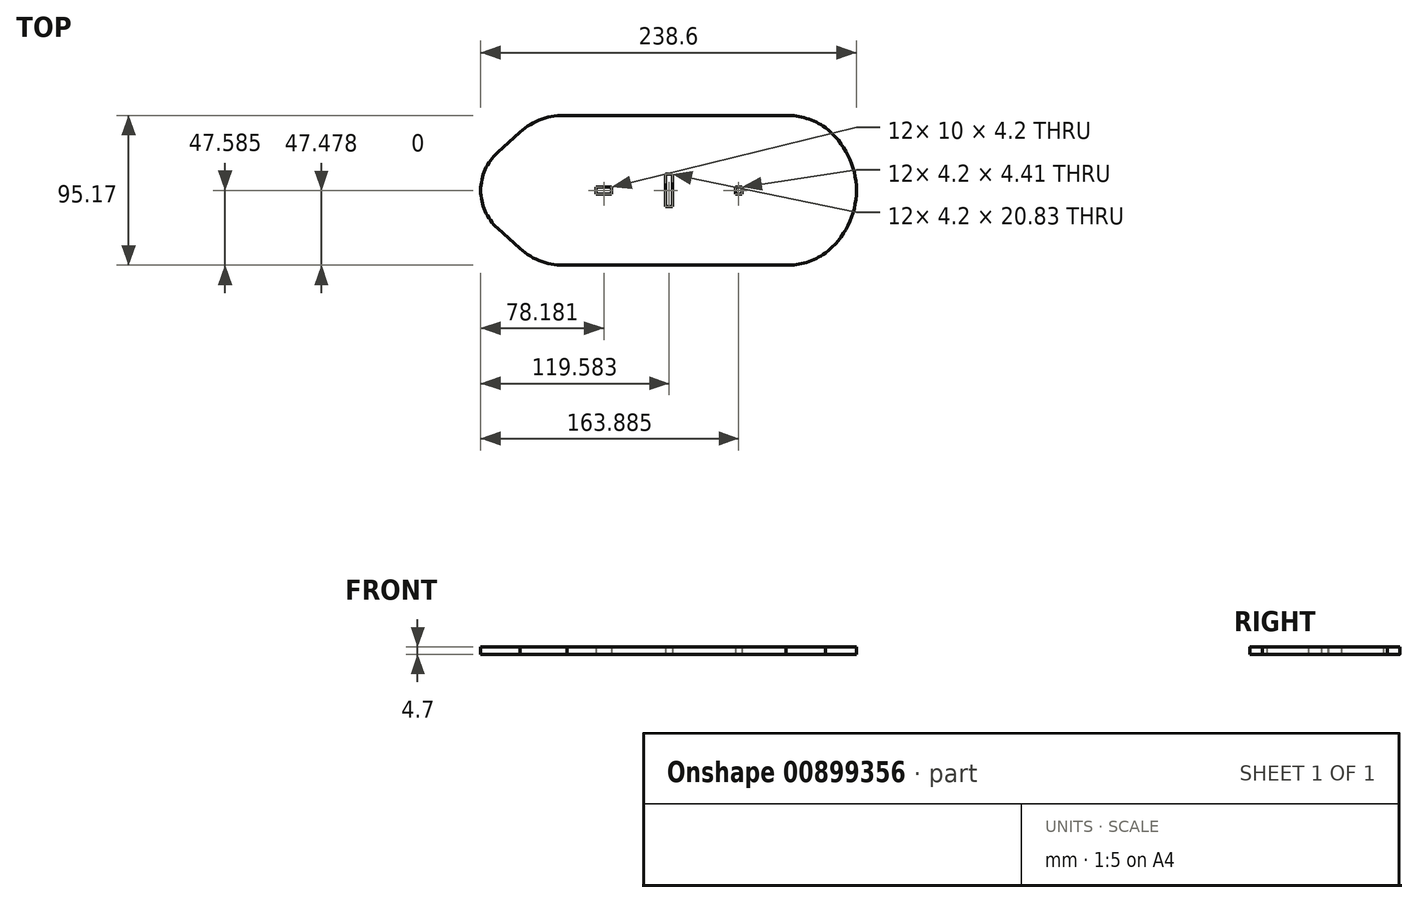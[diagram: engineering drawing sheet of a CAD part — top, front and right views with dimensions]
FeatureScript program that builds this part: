
annotation { "Feature Type Name" : "Feature", "Feature Type Description" : "" }
export const myFeature = defineFeature(function(context is Context, id is Id, definition is map)
    precondition{}
    {
        {
            var Q0;
            Q0=qCreatedBy(makeId("Top.planeOp"),FACE);
            var sketch = newSketch(context, id + "F0", { "sketchPlane" : qUnion([Q0])});
            skPoint(sketch, "E0.middle", {"position": v(7.5, -191.73) * mm});
            skPoint(sketch, "E1.endSnap0", {"position": v(-67.5, -191.73) * mm});
            skPoint(sketch, "E2", {"position": v(3.8, -191.73) * mm});
            skPoint(sketch, "E3.orphan", {"position": v(-86.92, -191.73) * mm});
            skPoint(sketch, "E4", {"position": v(-37.6, -191.83) * mm});
            skPoint(sketch, "E5", {"position": v(48.31, -191.73) * mm});
            skLineSegment(sketch, "E6.bottom", {"start": v(-42.6, -189.73) * mm, "end": v(-32.6, -189.73) * mm});
            skLineSegment(sketch, "E6.top", {"start": v(-42.6, -193.93) * mm, "end": v(-32.6, -193.93) * mm});
            skLineSegment(sketch, "E6.left", {"start": v(-42.6, -189.73) * mm, "end": v(-42.6, -193.93) * mm});
            skLineSegment(sketch, "E6.right", {"start": v(-32.6, -189.73) * mm, "end": v(-32.6, -193.93) * mm});
            skLineSegment(sketch, "E7.MirrorCS", {"start": v(46, -189.52) * mm, "end": v(46, -193.93) * mm});
            skLineSegment(sketch, "E8.MirrorCS", {"start": v(50.2, -189.52) * mm, "end": v(46, -189.52) * mm});
            skLineSegment(sketch, "E9.MirrorCS", {"start": v(50.2, -189.52) * mm, "end": v(50.2, -193.93) * mm});
            skLineSegment(sketch, "E10.MirrorCS", {"start": v(50.2, -193.93) * mm, "end": v(46, -193.93) * mm});
            skLineSegment(sketch, "E11.bottom", {"start": v(1.7, -181.3) * mm, "end": v(5.9, -181.3) * mm});
            skLineSegment(sketch, "E11.top", {"start": v(1.7, -202.14) * mm, "end": v(5.9, -202.14) * mm});
            skLineSegment(sketch, "E11.left", {"start": v(1.7, -181.3) * mm, "end": v(1.7, -202.14) * mm});
            skLineSegment(sketch, "E11.right", {"start": v(5.9, -181.3) * mm, "end": v(5.9, -202.14) * mm});
            skPoint(sketch, "E12.orphan", {"position": v(-67.5, -174.23) * mm});
            skPoint(sketch, "E13.orphan", {"position": v(-67.5, -209.23) * mm});
            skArc(sketch, "E14.4", {"start": v(88.21, -172.03) * mm, "mid": v(88.18, -172) * mm, "end": v(88.15, -171.97) * mm});
            skArc(sketch, "E15.0", {"start": v(-60.93, -144.23) * mm, "mid": v(-76.9, -146.42) * mm, "end": v(-90.7, -154.74) * mm});
            skLineSegment(sketch, "E15.1", {"start": v(-90.7, -154.74) * mm, "end": v(-105.1, -167.71) * mm});
            skLineSegment(sketch, "E15.2", {"start": v(-60.93, -144.23) * mm, "end": v(78.12, -144.23) * mm});
            skArc(sketch, "E15.3", {"start": v(-105.1, -167.71) * mm, "mid": v(-115.78, -191.73) * mm, "end": v(-105.1, -215.74) * mm});
            skLineSegment(sketch, "E15.4", {"start": v(-105.1, -215.74) * mm, "end": v(-90.7, -228.7) * mm});
            skArc(sketch, "E15.5", {"start": v(-60.93, -239.23) * mm, "mid": v(-76.9, -237.03) * mm, "end": v(-90.7, -228.7) * mm});
            skArc(sketch, "E15.6", {"start": v(103.07, -151.92) * mm, "mid": v(91.24, -145.98) * mm, "end": v(78.12, -144.23) * mm});
            skArc(sketch, "E15.7", {"start": v(103.07, -231.53) * mm, "mid": v(122.82, -191.73) * mm, "end": v(103.07, -151.92) * mm});
            skArc(sketch, "E15.8", {"start": v(103.07, -231.53) * mm, "mid": v(91.24, -237.47) * mm, "end": v(78.12, -239.23) * mm});
            skLineSegment(sketch, "E15.9", {"start": v(-60.93, -239.23) * mm, "end": v(78.12, -239.23) * mm});
            skLineSegment(sketch, "E16.trimOffspring", {"start": v(82.5, -208.77) * mm, "end": v(82.5, -209.23) * mm});
            skPoint(sketch, "E17.MirrorCS.end.orphan", {"position": v(78.78, -209.23) * mm});
            skPoint(sketch, "E18.orphan", {"position": v(85.17, -207.46) * mm});
            skPoint(sketch, "E19.orphan", {"position": v(85.17, -176) * mm});
            skPoint(sketch, "E20.end.orphan", {"position": v(78.78, -174.23) * mm});
            skSolve(sketch);
        }
        {
            var Q0;
            Q0 = qSketchRegion(id + "F0", true);
            extrude(context, id + "F1", {"entities" : qUnion([Q0]), "depth" : 4.7 * mm, "offsetDistance" : 25 * mm});
        }
    });
